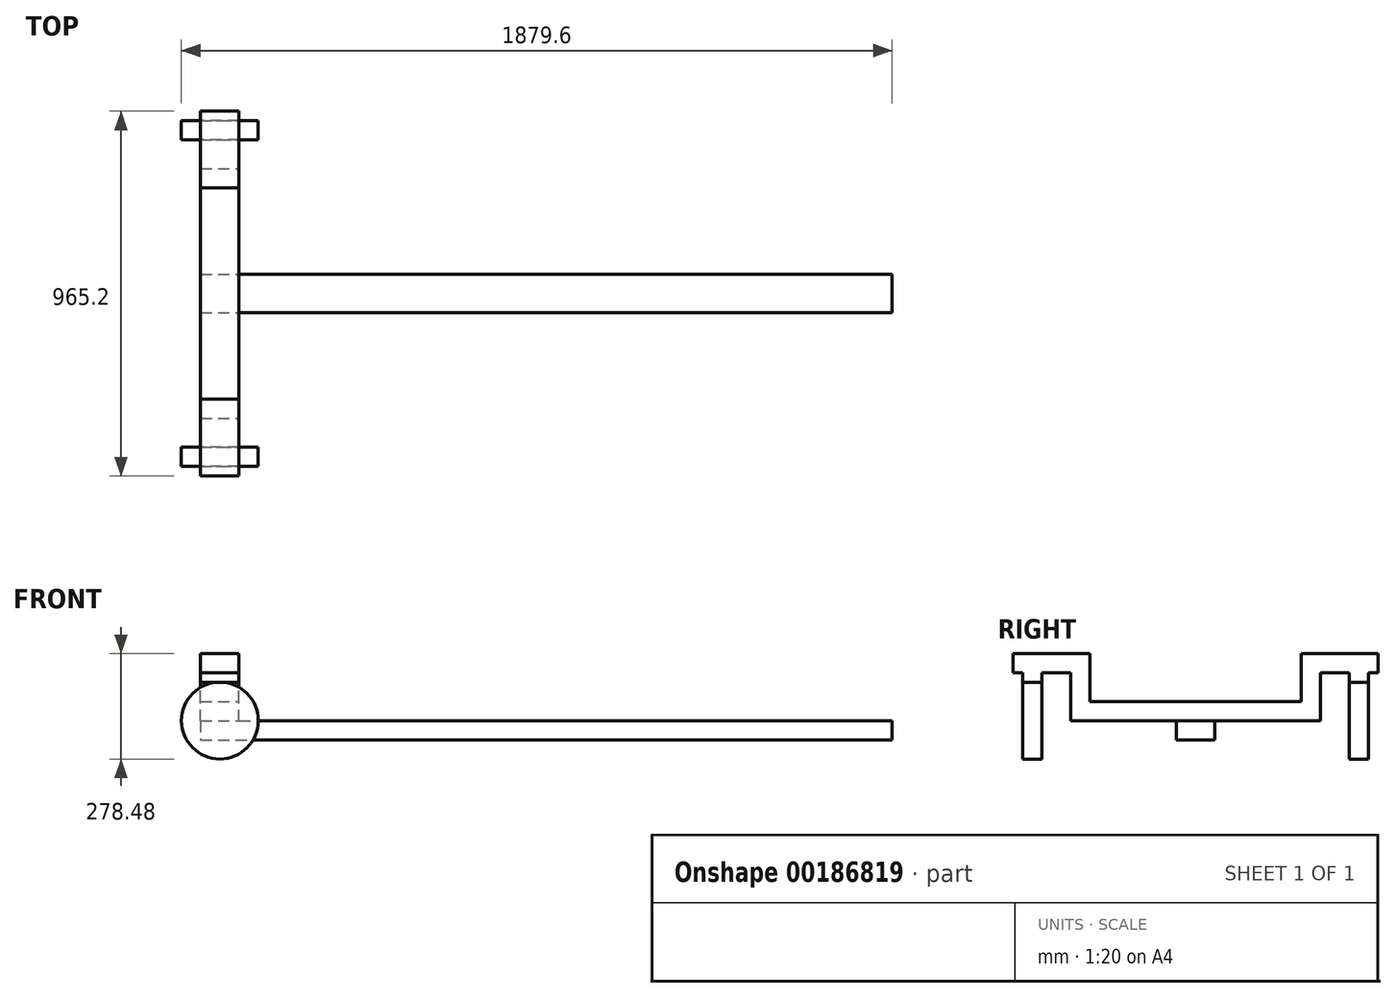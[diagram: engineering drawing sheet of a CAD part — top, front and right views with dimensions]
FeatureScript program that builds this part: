
annotation { "Feature Type Name" : "Feature", "Feature Type Description" : "" }
export const myFeature = defineFeature(function(context is Context, id is Id, definition is map)
    precondition{}
    {
        {
            var Q0;
            Q0=qCreatedBy(makeId("Top.planeOp"),FACE);
            var sketch = newSketch(context, id + "F0", { "sketchPlane" : qUnion([Q0])});
            skLineSegment(sketch, "E0.bottom", {"start": v(-914.4, -50.8) * mm, "end": v(914.4, -50.8) * mm});
            skLineSegment(sketch, "E0.top", {"start": v(-914.4, 50.8) * mm, "end": v(914.4, 50.8) * mm});
            skLineSegment(sketch, "E0.left", {"start": v(-914.4, -50.8) * mm, "end": v(-914.4, 50.8) * mm});
            skLineSegment(sketch, "E0.right", {"start": v(914.4, -50.8) * mm, "end": v(914.4, 50.8) * mm});
            skSolve(sketch);
        }
        {
            var Q0;
            Q0=makeQuery(id+"F0.imprint","IMPRINT",FACE,{"disambiguationData":[TD([[makeQuery(id+"F0.imprint","IMPRINT",EDGE,{"derivedFrom":sQuery(id+"F0.wireOp",EDGE,"E0.bottom")}),1.0]])]});
            extrude(context, id + "F1", {"entities" : qUnion([Q0]), "depth" : 50.8 * mm});
        }
        {
            var Q0;
            Q0=makeQuery(id+"F1.opExtrude","CAP_FACE",FACE,{"disambiguationData":[OSD([sQuery(id+"F0.wireOp",EDGE,"E0.bottom"),sQuery(id+"F0.wireOp",EDGE,"E0.top"),sQuery(id+"F0.wireOp",EDGE,"E0.left"),sQuery(id+"F0.wireOp",EDGE,"E0.right")])],"isStart":false});
            var sketch = newSketch(context, id + "F2", { "sketchPlane" : qUnion([Q0])});
            skLineSegment(sketch, "E1.bottom", {"start": v(-914.4, 228.6) * mm, "end": v(-812.8, 228.6) * mm});
            skLineSegment(sketch, "E1.top", {"start": v(-914.4, -279.4) * mm, "end": v(-812.8, -279.4) * mm});
            skLineSegment(sketch, "E1.left", {"start": v(-914.4, 228.6) * mm, "end": v(-914.4, -279.4) * mm});
            skLineSegment(sketch, "E1.right", {"start": v(-812.8, 228.6) * mm, "end": v(-812.8, -279.4) * mm});
            skSolve(sketch);
        }
        {
            var Q0;
            {var subQ0=sQuery(id+"F2.wireOp",EDGE,"E1.bottom");Q0=makeQuery(id+"F2.imprint","IMPRINT",FACE,{"disambiguationData":[TD([[makeQuery(id+"F2.imprint","IMPRINT",EDGE,{"derivedFrom":subQ0}),-1.0]])]});}
            var Q1;
            {var subQ0=sQuery(id+"F2.wireOp",EDGE,"E1.left");var subQ1=makeQuery(id+"F1.opExtrude","CAP_EDGE",EDGE,{"disambiguationData":[OSD([sQuery(id+"F0.wireOp",EDGE,"E0.bottom")])],"isStart":false});var subQ2=makeQuery(id+"F2.imprint","INTERSECT",VERTEX,{"derivedFrom":[subQ1,subQ0]});var subQ3=makeQuery(id+"F1.opExtrude","CAP_EDGE",EDGE,{"disambiguationData":[OSD([sQuery(id+"F0.wireOp",EDGE,"E0.top")])],"isStart":false});var subQ4=makeQuery(id+"F2.imprint","INTERSECT",VERTEX,{"derivedFrom":[subQ3,subQ0]});Q1=makeQuery(id+"F2.imprint","IMPRINT",FACE,{"disambiguationData":[TD([[makeQuery(id+"F2.imprint","IMPRINT",EDGE,{"disambiguationData":[TD([[subQ2,-1.0],[subQ4,1.0]])],"derivedFrom":subQ0}),-1.0]])]});}
            var Q2;
            {var subQ0=sQuery(id+"F2.wireOp",EDGE,"E1.top");Q2=makeQuery(id+"F2.imprint","IMPRINT",FACE,{"disambiguationData":[TD([[makeQuery(id+"F2.imprint","IMPRINT",EDGE,{"derivedFrom":subQ0}),1.0]])]});}
            extrude(context, id + "F3", {"entities" : qUnion([Q0, Q1, Q2]), "operationType" : NewBodyOperationType.ADD, "depth" : 50.8 * mm});
        }
        {
            var Q0;
            Q0=makeQuery(id+"F3.opExtrude","SWEPT_FACE",FACE,{"disambiguationData":[OSD([sQuery(id+"F2.wireOp",EDGE,"E1.top")])]});
            var sketch = newSketch(context, id + "F4", { "sketchPlane" : qUnion([Q0])});
            skLineSegment(sketch, "E2.bottom", {"start": v(-914.4, 50.8) * mm, "end": v(-812.8, 50.8) * mm});
            skLineSegment(sketch, "E2.top", {"start": v(-914.4, 177.8) * mm, "end": v(-812.8, 177.8) * mm});
            skLineSegment(sketch, "E2.left", {"start": v(-914.4, 50.8) * mm, "end": v(-914.4, 177.8) * mm});
            skLineSegment(sketch, "E2.right", {"start": v(-812.8, 50.8) * mm, "end": v(-812.8, 177.8) * mm});
            skSolve(sketch);
        }
        {
            var Q0;
            {var subQ0=sQuery(id+"F4.wireOp",EDGE,"E2.top");Q0=makeQuery(id+"F4.imprint","IMPRINT",FACE,{"disambiguationData":[TD([[makeQuery(id+"F4.imprint","IMPRINT",EDGE,{"derivedFrom":subQ0}),-1.0]])]});}
            var Q1;
            {var subQ0=sQuery(id+"F4.wireOp",EDGE,"E2.bottom");Q1=makeQuery(id+"F4.imprint","IMPRINT",FACE,{"disambiguationData":[TD([[makeQuery(id+"F4.imprint","IMPRINT",EDGE,{"derivedFrom":subQ0}),1.0]])]});}
            extrude(context, id + "F5", {"entities" : qUnion([Q0, Q1]), "operationType" : NewBodyOperationType.ADD, "depth" : 50.8 * mm});
        }
        {
            var Q0;
            Q0=makeQuery(id+"F5.opExtrude","SWEPT_FACE",FACE,{"disambiguationData":[OSD([sQuery(id+"F4.wireOp",EDGE,"E2.top")])]});
            var sketch = newSketch(context, id + "F6", { "sketchPlane" : qUnion([Q0])});
            skLineSegment(sketch, "E3.bottom", {"start": v(-914.4, -279.4) * mm, "end": v(-812.8, -279.4) * mm});
            skLineSegment(sketch, "E3.top", {"start": v(-914.4, -482.6) * mm, "end": v(-812.8, -482.6) * mm});
            skLineSegment(sketch, "E3.left", {"start": v(-914.4, -279.4) * mm, "end": v(-914.4, -482.6) * mm});
            skLineSegment(sketch, "E3.right", {"start": v(-812.8, -279.4) * mm, "end": v(-812.8, -482.6) * mm});
            skSolve(sketch);
        }
        {
            var Q0;
            {var subQ0=sQuery(id+"F6.wireOp",EDGE,"E3.top");Q0=makeQuery(id+"F6.imprint","IMPRINT",FACE,{"disambiguationData":[TD([[makeQuery(id+"F6.imprint","IMPRINT",EDGE,{"derivedFrom":subQ0}),1.0]])]});}
            var Q1;
            {var subQ0=sQuery(id+"F6.wireOp",EDGE,"E3.bottom");Q1=makeQuery(id+"F6.imprint","IMPRINT",FACE,{"disambiguationData":[TD([[makeQuery(id+"F6.imprint","IMPRINT",EDGE,{"derivedFrom":subQ0}),-1.0]])]});}
            extrude(context, id + "F7", {"entities" : qUnion([Q0, Q1]), "operationType" : NewBodyOperationType.ADD, "depth" : 50.8 * mm});
        }
        {
            var Q0;
            Q0=makeQuery(id+"F5.opExtrude","CAP_FACE",FACE,{"disambiguationData":[OSD([sQuery(id+"F4.wireOp",EDGE,"E2.bottom"),sQuery(id+"F4.wireOp",EDGE,"E2.top"),sQuery(id+"F4.wireOp",EDGE,"E2.left"),sQuery(id+"F4.wireOp",EDGE,"E2.right")])],"isStart":false});
            cPlane(context, id + "F8", {"entities" : qUnion([Q0]), "cplaneType" : CPlaneType.OFFSET, "offset" : 127 * mm, "width" : 152.4 * mm, "height" : 152.4 * mm});
        }
        {
            var Q0;
            Q0=qCreatedBy(id+"F8.planeOp",FACE);
            var sketch = newSketch(context, id + "F9", { "sketchPlane" : qUnion([Q0])});
            skLineSegment(sketch, "E4.bottom", {"start": v(-914.4, 177.8) * mm, "end": v(-812.8, 177.8) * mm});
            skLineSegment(sketch, "E4.top", {"start": v(-914.4, 153.32) * mm, "end": v(-812.8, 153.32) * mm});
            skLineSegment(sketch, "E4.left", {"start": v(-914.4, 177.8) * mm, "end": v(-914.4, 153.32) * mm});
            skLineSegment(sketch, "E4.right", {"start": v(-812.8, 177.8) * mm, "end": v(-812.8, 153.32) * mm});
            skCircle(sketch, "E5", {"center": v(-863.6, 51.72) * mm, "radius": 101.6 * mm});
            skPoint(sketch, "E5.centerSnap0", {"position": v(-863.6, 153.32) * mm});
            skSolve(sketch);
        }
        {
            var Q0;
            Q0=makeQuery(id+"F9.imprint","IMPRINT",FACE,{"disambiguationData":[TD([[makeQuery(id+"F9.imprint","IMPRINT",EDGE,{"derivedFrom":sQuery(id+"F9.wireOp",EDGE,"E5")}),1.0]])]});
            var Q1;
            Q1=makeQuery(id+"F9.imprint","IMPRINT",FACE,{"disambiguationData":[TD([[makeQuery(id+"F9.imprint","IMPRINT",EDGE,{"derivedFrom":sQuery(id+"F9.wireOp",EDGE,"E4.bottom")}),-1.0]])]});
            extrude(context, id + "F10", {"entities" : qUnion([Q0, Q1]), "oppositeDirection" : true, "depth" : 50.8 * mm});
        }
        {
            var Q0;
            Q0=makeQuery(id+"F1.opExtrude","SWEPT_BODY",BODY,{"disambiguationData":[OSD([sQuery(id+"F0.wireOp",EDGE,"E0.bottom"),sQuery(id+"F0.wireOp",EDGE,"E0.top"),sQuery(id+"F0.wireOp",EDGE,"E0.left"),sQuery(id+"F0.wireOp",EDGE,"E0.right")])]});
            var Q1;
            Q1=makeQuery(id+"F10.opExtrude","SWEPT_BODY",BODY,{"disambiguationData":[OSD([sQuery(id+"F9.wireOp",EDGE,"E5")])]});
            var Q2;
            Q2=makeQuery(id+"F10.opExtrude","SWEPT_BODY",BODY,{"disambiguationData":[OSD([sQuery(id+"F9.wireOp",EDGE,"E4.bottom"),sQuery(id+"F9.wireOp",EDGE,"E4.top"),sQuery(id+"F9.wireOp",EDGE,"E4.left"),sQuery(id+"F9.wireOp",EDGE,"E4.right")])]});
            var Q3;
            Q3=qCreatedBy(makeId("Front.planeOp"),FACE);
            mirror(context, id + "F11", {"operationType" : NewBodyOperationType.ADD, "entities" : qUnion([Q0, Q1, Q2]), "mirrorPlane" : qUnion([Q3])});
        }
    });
